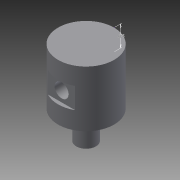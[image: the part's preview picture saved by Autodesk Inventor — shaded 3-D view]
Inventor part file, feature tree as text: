
AUTODESK INVENTOR PART (.ipt)
format: ipt  version: 2014 SP1 (Build 180222100, 222)  size: 103,424 bytes
history: native  units: in
note: dims shown in document units (in); Inventor stores cm internally (conversion verified against a paired STEP export)
features: sketch x4, extrude x2, revolve x1, projected_geometry x1
ambient origin geometry x8: Origin, YZ Plane, XZ Plane, XY Plane, X Axis, Y Axis, Z Axis, Center Point
bodies: Solid1 (feature_tree)
feature tree (8):
  revolve  "Revolution1"  [1 undecoded]
  extrude  "Extrusion1"  Depth=1.0in
  extrude  "Extrusion2"  Depth=0.25in
  sketch  "Sketch4"  dims[d6=1.0in d7=0.0in d9=0.0625in d10=0.0625in d11=0.375in d12=1.0in d13=0.0in d14=0.375in]
  sketch  "Sketch1"  dims[d0=1.5in d1=0.5in]
  sketch  "Sketch2"  dims[d2=1.0in d3=0.325in]
  sketch  "Sketch3"  dims[d4=90.0deg d5=0.25in]
  projected_geometry  "Project Cut Edges1"
note: 1 required parameter value undecoded (feature->parameter linkage not recoverable at this tier; creation-order binding heuristic only, values carry confidence <= 0.55)
